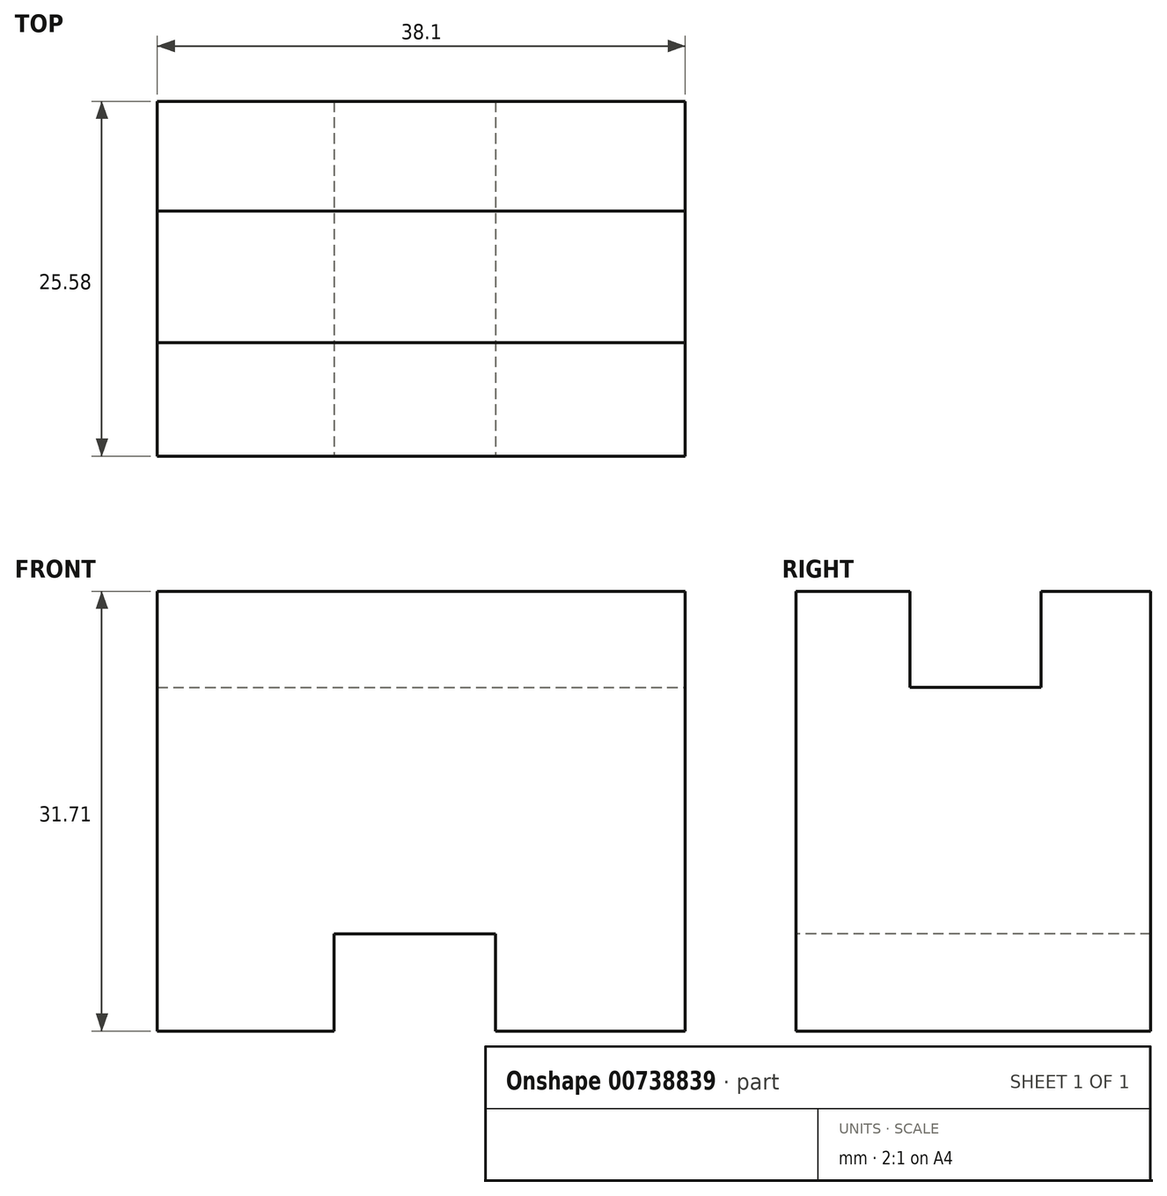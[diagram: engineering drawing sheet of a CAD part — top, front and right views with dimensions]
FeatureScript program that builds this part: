
annotation { "Feature Type Name" : "Feature", "Feature Type Description" : "" }
export const myFeature = defineFeature(function(context is Context, id is Id, definition is map)
    precondition{}
    {
        {
            var Q0;
            Q0=qCreatedBy(makeId("Right.planeOp"),FACE);
            var sketch = newSketch(context, id + "F0", { "sketchPlane" : qUnion([Q0])});
            skLineSegment(sketch, "E0", {"start": v(0, 0) * mm, "end": v(25.58, 0) * mm});
            skLineSegment(sketch, "E1", {"start": v(25.58, 0) * mm, "end": v(25.58, 31.7) * mm});
            skLineSegment(sketch, "E2", {"start": v(25.58, 31.7) * mm, "end": v(0, 31.7) * mm});
            skLineSegment(sketch, "E3", {"start": v(0, 31.7) * mm, "end": v(0, 0) * mm});
            skSolve(sketch);
        }
        {
            var Q0;
            Q0 = qSketchRegion(id + "F0", true);
            var Q1;
            Q1=makeQuery(id+"F0.imprint","IMPRINT",FACE,{"disambiguationData":[TD([[makeQuery(id+"F0.imprint","IMPRINT",EDGE,{"derivedFrom":sQuery(id+"F0.wireOp",EDGE,"E0")}),1.0]])]});
            extrude(context, id + "F1", {"entities" : qUnion([Q0, Q1]), "depth" : 38.1 * mm, "offsetDistance" : 25.4 * mm});
        }
        {
            var Q0;
            Q0=makeQuery(id+"F1.opExtrude","CAP_FACE",FACE,{"disambiguationData":[OSD([sQuery(id+"F0.wireOp",EDGE,"E0"),sQuery(id+"F0.wireOp",EDGE,"E1"),sQuery(id+"F0.wireOp",EDGE,"E2"),sQuery(id+"F0.wireOp",EDGE,"E3")])],"isStart":false});
            var sketch = newSketch(context, id + "F2", { "sketchPlane" : qUnion([Q0])});
            skLineSegment(sketch, "E4", {"start": v(8.2, 31.7) * mm, "end": v(8.2, 24.8) * mm});
            skLineSegment(sketch, "E5", {"start": v(8.2, 24.8) * mm, "end": v(17.68, 24.8) * mm});
            skLineSegment(sketch, "E6", {"start": v(17.68, 24.8) * mm, "end": v(17.68, 31.7) * mm});
            skSolve(sketch);
        }
        {
            var Q0;
            {var subQ0=sQuery(id+"F2.wireOp",EDGE,"E4");Q0=makeQuery(id+"F2.imprint","IMPRINT",FACE,{"disambiguationData":[TD([[makeQuery(id+"F2.imprint","IMPRINT",EDGE,{"derivedFrom":subQ0}),1.0]])]});}
            extrude(context, id + "F3", {"entities" : qUnion([Q0]), "operationType" : NewBodyOperationType.REMOVE, "oppositeDirection" : true, "depth" : 38.1 * mm, "offsetDistance" : 25.4 * mm});
        }
        {
            var Q0;
            Q0=makeQuery(id+"F1.opExtrude","SWEPT_FACE",FACE,{"disambiguationData":[OSD([sQuery(id+"F0.wireOp",EDGE,"E3")])]});
            var sketch = newSketch(context, id + "F4", { "sketchPlane" : qUnion([Q0])});
            skLineSegment(sketch, "E7", {"start": v(12.74, 0) * mm, "end": v(12.74, 7.01) * mm});
            skLineSegment(sketch, "E8", {"start": v(12.74, 7.01) * mm, "end": v(24.4, 7.01) * mm});
            skLineSegment(sketch, "E9", {"start": v(24.4, 7.01) * mm, "end": v(24.4, 0) * mm});
            skLineSegment(sketch, "E10", {"start": v(24.4, 0) * mm, "end": v(12.74, 0) * mm});
            skSolve(sketch);
        }
        {
            var Q0;
            Q0=makeQuery(id+"F4.imprint","IMPRINT",FACE,{"disambiguationData":[TD([[makeQuery(id+"F4.imprint","IMPRINT",EDGE,{"derivedFrom":sQuery(id+"F4.wireOp",EDGE,"E7")}),-1.0]])]});
            extrude(context, id + "F5", {"entities" : qUnion([Q0]), "operationType" : NewBodyOperationType.REMOVE, "oppositeDirection" : true, "depth" : 38.1 * mm, "offsetDistance" : 25.4 * mm});
        }
    });
